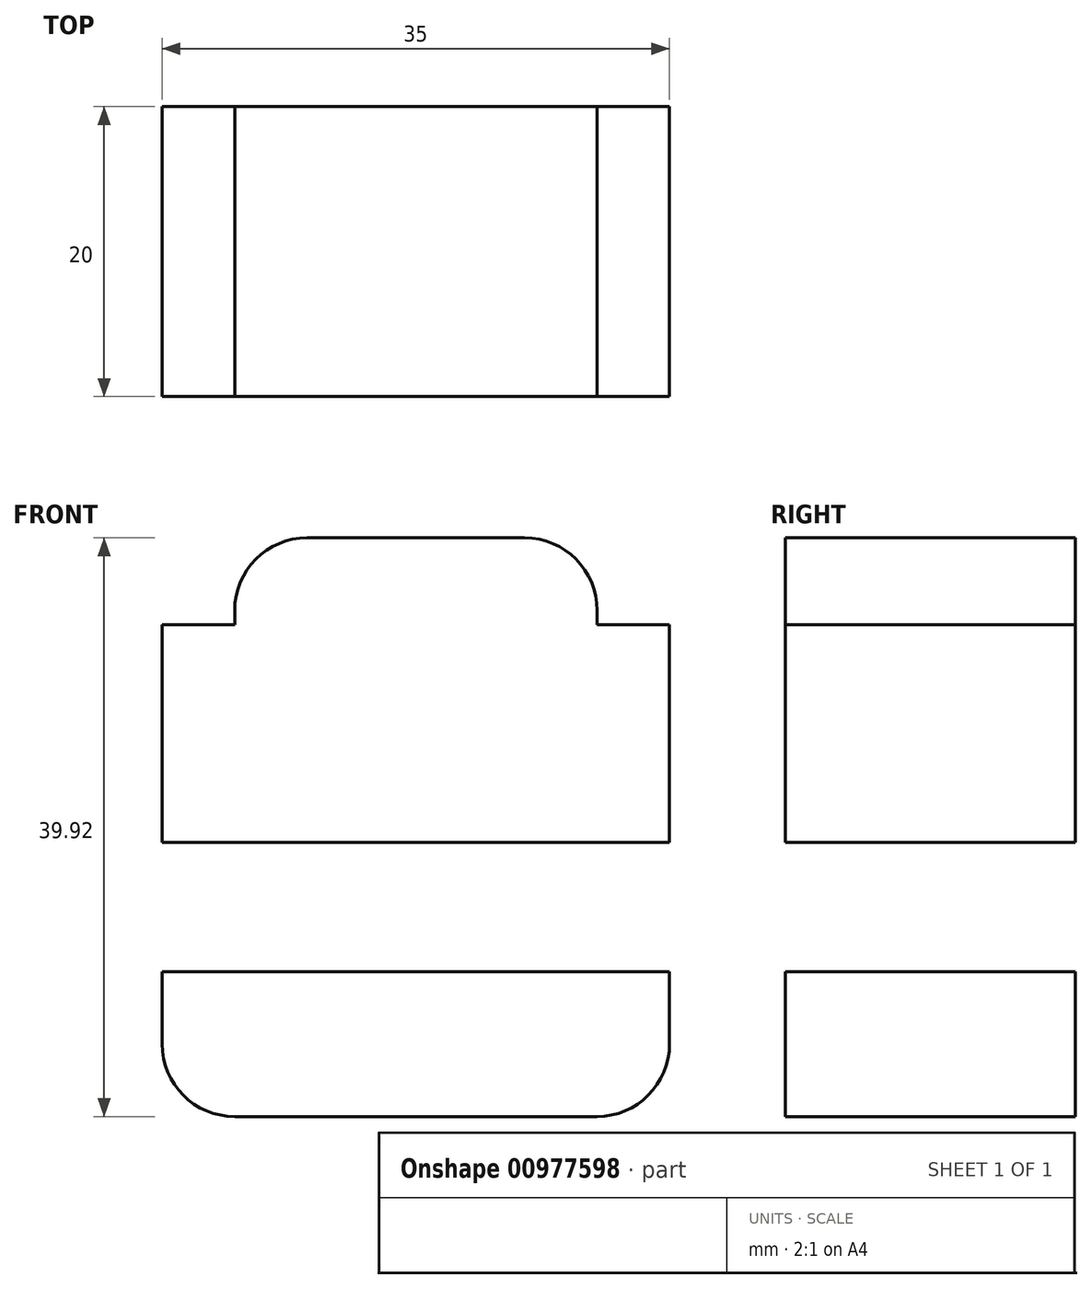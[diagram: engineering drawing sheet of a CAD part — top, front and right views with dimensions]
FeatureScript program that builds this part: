
annotation { "Feature Type Name" : "Feature", "Feature Type Description" : "" }
export const myFeature = defineFeature(function(context is Context, id is Id, definition is map)
    precondition{}
    {
        {
            var Q0;
            Q0=qCreatedBy(makeId("Front.planeOp"),FACE);
            var sketch = newSketch(context, id + "F0", { "sketchPlane" : qUnion([Q0])});
            skLineSegment(sketch, "E0.bottom", {"start": v(-68.54, 40.73) * mm, "end": v(-33.54, 40.73) * mm});
            skLineSegment(sketch, "E0.top", {"start": v(-63.54, 30.73) * mm, "end": v(-38.54, 30.73) * mm});
            skLineSegment(sketch, "E0.left", {"start": v(-68.54, 40.73) * mm, "end": v(-68.54, 35.73) * mm});
            skLineSegment(sketch, "E0.right", {"start": v(-33.54, 40.73) * mm, "end": v(-33.54, 35.73) * mm});
            skLineSegment(sketch, "E1", {"start": v(-68.54, 49.65) * mm, "end": v(-33.54, 49.65) * mm});
            skLineSegment(sketch, "E2", {"start": v(-33.54, 49.65) * mm, "end": v(-33.54, 64.65) * mm});
            skLineSegment(sketch, "E3", {"start": v(-33.54, 64.65) * mm, "end": v(-38.54, 64.65) * mm});
            skLineSegment(sketch, "E4", {"start": v(-38.54, 64.65) * mm, "end": v(-38.54, 65.65) * mm});
            skLineSegment(sketch, "E5", {"start": v(-43.54, 70.65) * mm, "end": v(-58.54, 70.65) * mm});
            skLineSegment(sketch, "E6", {"start": v(-63.54, 65.65) * mm, "end": v(-63.54, 64.65) * mm});
            skLineSegment(sketch, "E7", {"start": v(-63.54, 64.65) * mm, "end": v(-68.54, 64.65) * mm});
            skLineSegment(sketch, "E8", {"start": v(-68.54, 64.65) * mm, "end": v(-68.54, 49.65) * mm});
            skPoint(sketch, "E9.visualSharp", {"position": v(-63.54, 70.65) * mm});
            skArc(sketch, "E9.filletArc", {"start": v(-58.54, 70.65) * mm, "mid": v(-62.08, 69.18) * mm, "end": v(-63.54, 65.65) * mm});
            skPoint(sketch, "E10.visualSharp", {"position": v(-38.54, 70.65) * mm});
            skArc(sketch, "E10.filletArc", {"start": v(-38.54, 65.65) * mm, "mid": v(-40, 69.18) * mm, "end": v(-43.54, 70.65) * mm});
            skPoint(sketch, "E11.visualSharp", {"position": v(-33.54, 30.73) * mm});
            skArc(sketch, "E11.filletArc", {"start": v(-38.54, 30.73) * mm, "mid": v(-35, 32.2) * mm, "end": v(-33.54, 35.73) * mm});
            skPoint(sketch, "E12.visualSharp", {"position": v(-68.54, 30.73) * mm});
            skArc(sketch, "E12.filletArc", {"start": v(-68.54, 35.73) * mm, "mid": v(-67.08, 32.2) * mm, "end": v(-63.54, 30.73) * mm});
            skSolve(sketch);
        }
        {
            var Q0;
            Q0 = qSketchRegion(id + "F0", true);
            var Q1;
            Q1=makeQuery(id+"F0.imprint","IMPRINT",FACE,{"disambiguationData":[TD([[makeQuery(id+"F0.imprint","IMPRINT",EDGE,{"derivedFrom":sQuery(id+"F0.wireOp",EDGE,"E0.bottom")}),-1.0]])]});
            extrude(context, id + "F1", {"entities" : qUnion([Q0, Q1]), "depth" : 20 * mm, "offsetDistance" : 25 * mm});
        }
    });
